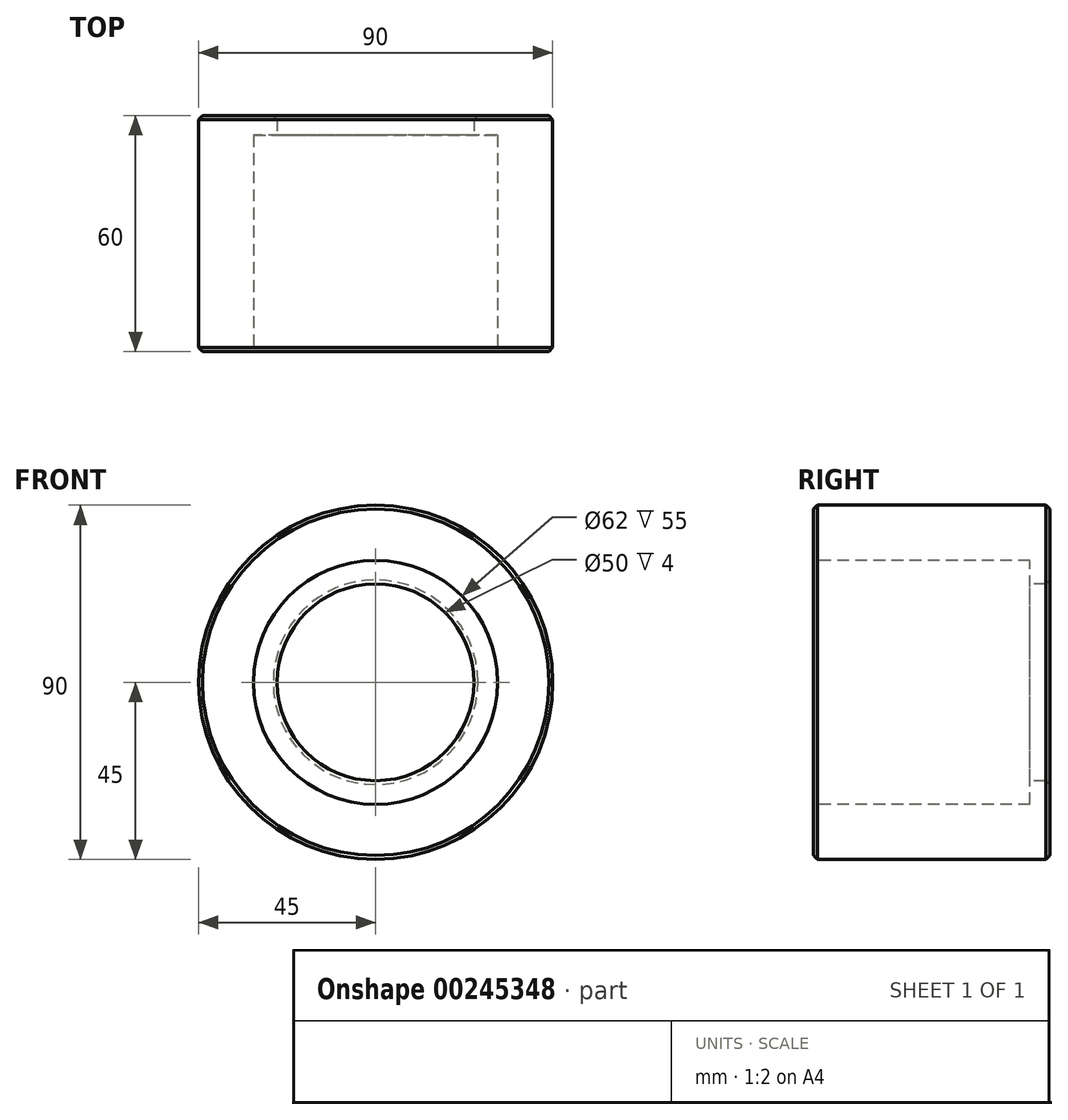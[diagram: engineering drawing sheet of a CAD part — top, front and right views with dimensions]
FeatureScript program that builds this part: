
annotation { "Feature Type Name" : "Feature", "Feature Type Description" : "" }
export const myFeature = defineFeature(function(context is Context, id is Id, definition is map)
    precondition{}
    {
        {
            var Q0;
            Q0=qCreatedBy(makeId("Front.planeOp"),FACE);
            var sketch = newSketch(context, id + "F0", { "sketchPlane" : qUnion([Q0])});
            skCircle(sketch, "E0", {"center": v(0, 0) * mm, "radius": 45 * mm});
            skSolve(sketch);
        }
        {
            var Q0;
            Q0=makeQuery(id+"F0.imprint","IMPRINT",FACE,{"disambiguationData":[TD([[makeQuery(id+"F0.imprint","IMPRINT",EDGE,{"derivedFrom":sQuery(id+"F0.wireOp",EDGE,"E0")}),1.0]])]});
            extrude(context, id + "F1", {"entities" : qUnion([Q0]), "depth" : 60 * mm});
        }
        {
            var Q0;
            Q0=makeQuery(id+"F1.opExtrude","CAP_FACE",FACE,{"disambiguationData":[OSD([sQuery(id+"F0.wireOp",EDGE,"E0")])],"isStart":false});
            var sketch = newSketch(context, id + "F2", { "sketchPlane" : qUnion([Q0])});
            skCircle(sketch, "E1", {"center": v(0, 0) * mm, "radius": 31 * mm});
            skSolve(sketch);
        }
        {
            var Q0;
            Q0 = qSketchRegion(id + "F2", true);
            extrude(context, id + "F3", {"entities" : qUnion([Q0]), "operationType" : NewBodyOperationType.REMOVE, "oppositeDirection" : true, "depth" : 55 * mm});
        }
        {
            var Q0;
            Q0=makeQuery(id+"F3.boolean.opBoolean","COPY",FACE,{"derivedFrom":makeQuery(id+"F3.opExtrude","CAP_FACE",FACE,{"disambiguationData":[OSD([sQuery(id+"F2.wireOp",EDGE,"E1")])],"isStart":false})});
            var sketch = newSketch(context, id + "F4", { "sketchPlane" : qUnion([Q0])});
            skCircle(sketch, "E2", {"center": v(0, 0) * mm, "radius": 25 * mm});
            skSolve(sketch);
        }
        {
            var Q0;
            Q0=makeQuery(id+"F4.imprint","IMPRINT",FACE,{"disambiguationData":[TD([[makeQuery(id+"F4.imprint","IMPRINT",EDGE,{"derivedFrom":sQuery(id+"F4.wireOp",EDGE,"E2")}),1.0]])]});
            extrude(context, id + "F5", {"entities" : qUnion([Q0]), "operationType" : NewBodyOperationType.REMOVE, "oppositeDirection" : true, "depth" : 25 * mm});
        }
        {
            var Q0;
            Q0=makeQuery(id+"F1.opExtrude","CAP_EDGE",EDGE,{"disambiguationData":[OSD([sQuery(id+"F0.wireOp",EDGE,"E0")])],"isStart":false});
            var Q1;
            Q1=makeQuery(id+"F3.boolean.opBoolean","COPY",EDGE,{"derivedFrom":makeQuery(id+"F3.opExtrude","CAP_EDGE",EDGE,{"disambiguationData":[OSD([sQuery(id+"F2.wireOp",EDGE,"E1")])],"isStart":true})});
            var Q2;
            Q2=makeQuery(id+"F5.boolean.opBoolean","INTERSECT",EDGE,{"derivedFrom":[makeQuery(id+"F1.opExtrude","CAP_FACE",FACE,{"disambiguationData":[OSD([sQuery(id+"F0.wireOp",EDGE,"E0")])],"isStart":true}),makeQuery(id+"F5.opExtrude","SWEPT_FACE",FACE,{"disambiguationData":[OSD([sQuery(id+"F4.wireOp",EDGE,"E2")])]})]});
            var Q3;
            Q3=makeQuery(id+"F5.boolean.opBoolean","COPY",EDGE,{"derivedFrom":makeQuery(id+"F5.opExtrude","CAP_EDGE",EDGE,{"disambiguationData":[OSD([sQuery(id+"F4.wireOp",EDGE,"E2")])],"isStart":true})});
            var Q4;
            Q4=makeQuery(id+"F1.opExtrude","CAP_EDGE",EDGE,{"disambiguationData":[OSD([sQuery(id+"F0.wireOp",EDGE,"E0")])],"isStart":true});
            chamfer(context, id + "F6", {"entities" : qUnion([Q0, Q1, Q2, Q3, Q4]), "width" : 1 * mm, "tangentPropagation" : true});
        }
    });
